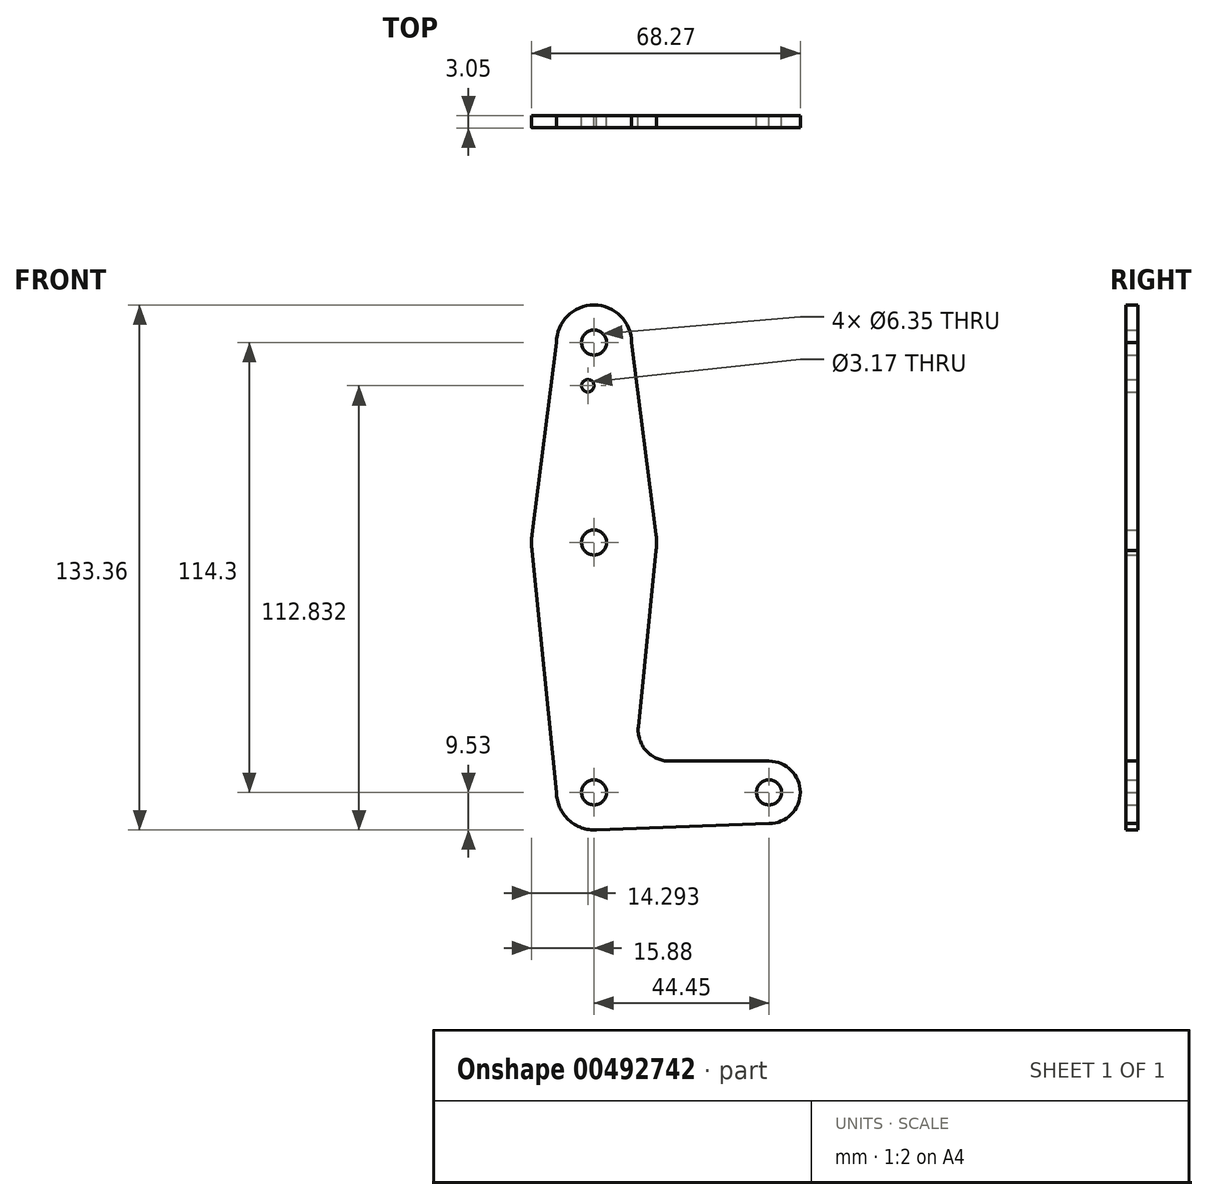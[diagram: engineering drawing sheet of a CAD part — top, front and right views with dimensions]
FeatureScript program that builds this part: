
annotation { "Feature Type Name" : "Feature", "Feature Type Description" : "" }
export const myFeature = defineFeature(function(context is Context, id is Id, definition is map)
    precondition{}
    {
        {
            var Q0;
            Q0=qCreatedBy(makeId("Front.planeOp"),FACE);
            var sketch = newSketch(context, id + "F0", { "sketchPlane" : qUnion([Q0])});
            skLineSegment(sketch, "E0", {"start": v(0, 0) * mm, "end": v(0, 114.3) * mm, "construction": true});
            skLineSegment(sketch, "E1", {"start": v(44.45, 0) * mm, "end": v(0, 0) * mm, "construction": true});
            skCircle(sketch, "E2", {"center": v(44.45, 0) * mm, "radius": 7.94 * mm});
            skCircle(sketch, "E3", {"center": v(0, 0) * mm, "radius": 9.53 * mm});
            skCircle(sketch, "E4", {"center": v(0, 114.3) * mm, "radius": 9.53 * mm});
            skCircle(sketch, "E5", {"center": v(0, 63.5) * mm, "radius": 15.88 * mm});
            skLineSegment(sketch, "E6", {"start": v(-9.53, 114.3) * mm, "end": v(-15.75, 65.5) * mm});
            skLineSegment(sketch, "E7", {"start": v(-9.52, 0) * mm, "end": v(-15.75, 61.5) * mm});
            skLineSegment(sketch, "E8", {"start": v(9.52, 114.3) * mm, "end": v(15.75, 65.5) * mm});
            skLineSegment(sketch, "E9", {"start": v(11.25, 16.68) * mm, "end": v(15.75, 61.5) * mm});
            skLineSegment(sketch, "E10", {"start": v(19.16, 7.94) * mm, "end": v(44.45, 7.94) * mm});
            skLineSegment(sketch, "E11", {"start": v(0, -9.53) * mm, "end": v(44.45, -7.94) * mm});
            skArc(sketch, "E12.filletArc", {"start": v(11.25, 16.68) * mm, "mid": v(13.26, 10.55) * mm, "end": v(19.16, 7.94) * mm});
            skCircle(sketch, "E13", {"center": v(0, 114.3) * mm, "radius": 3.18 * mm});
            skCircle(sketch, "E14", {"center": v(0, 63.5) * mm, "radius": 3.18 * mm});
            skCircle(sketch, "E15", {"center": v(0, 0) * mm, "radius": 3.18 * mm});
            skCircle(sketch, "E16", {"center": v(44.45, 0) * mm, "radius": 3.18 * mm});
            skCircle(sketch, "E17", {"center": v(-1.59, 103.3) * mm, "radius": 1.59 * mm});
            skSolve(sketch);
        }
        {
            var Q0;
            Q0 = qSketchRegion(id + "F0", true);
            extrude(context, id + "F1", {"entities" : qUnion([Q0]), "depth" : 3.05 * mm});
        }
    });
